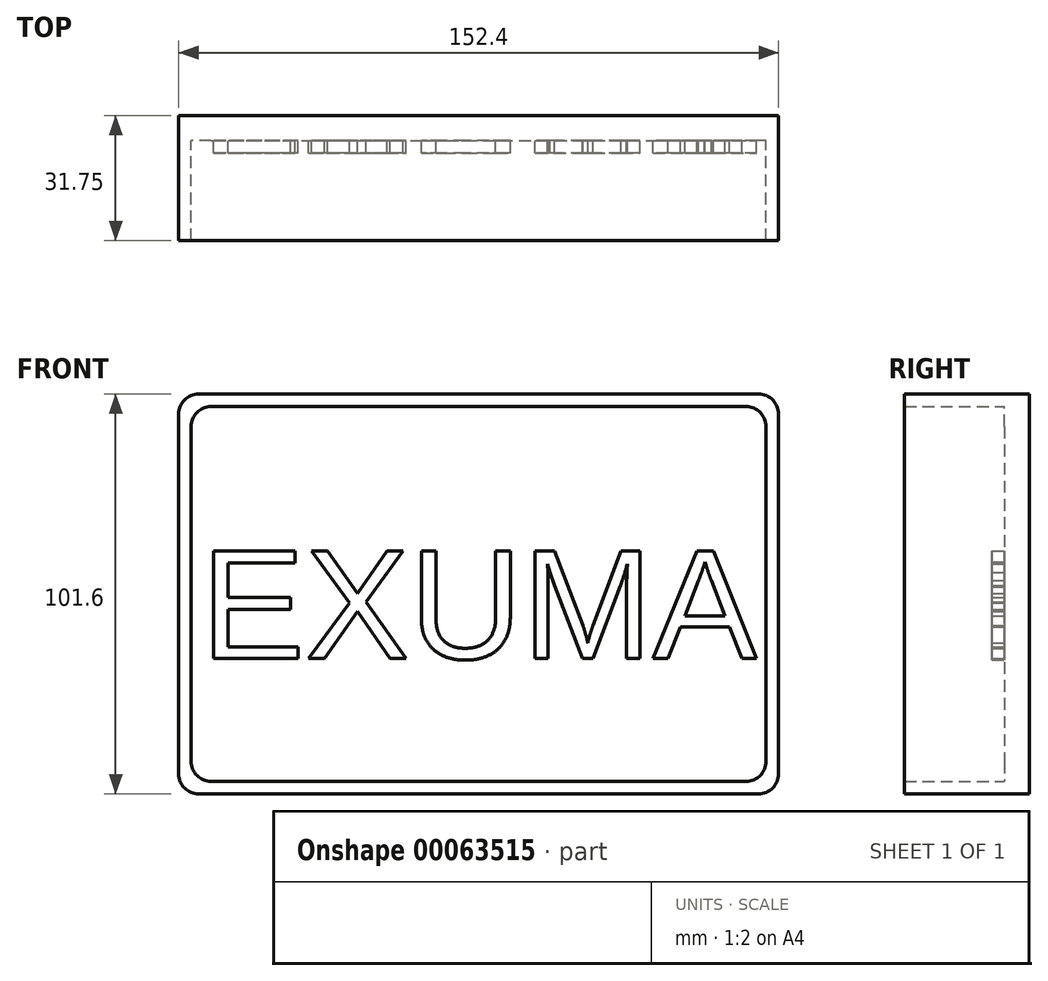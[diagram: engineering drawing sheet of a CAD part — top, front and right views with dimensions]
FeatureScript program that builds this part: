
annotation { "Feature Type Name" : "Feature", "Feature Type Description" : "" }
export const myFeature = defineFeature(function(context is Context, id is Id, definition is map)
    precondition{}
    {
        {
            var Q0;
            Q0=qCreatedBy(makeId("Front.planeOp"),FACE);
            var sketch = newSketch(context, id + "F0", { "sketchPlane" : qUnion([Q0])});
            skLineSegment(sketch, "E0.bottom", {"start": v(-70.07, 52.66) * mm, "end": v(82.33, 52.66) * mm});
            skLineSegment(sketch, "E0.top", {"start": v(-70.07, -48.94) * mm, "end": v(82.33, -48.94) * mm});
            skLineSegment(sketch, "E0.left", {"start": v(-70.07, 52.66) * mm, "end": v(-70.07, -48.94) * mm});
            skLineSegment(sketch, "E0.right", {"start": v(82.33, 52.66) * mm, "end": v(82.33, -48.94) * mm});
            skSolve(sketch);
        }
        {
            var Q0;
            Q0 = qSketchRegion(id + "F0", true);
            extrude(context, id + "F1", {"entities" : qUnion([Q0]), "depth" : 6.35 * mm});
        }
        {
            var Q0;
            Q0=makeQuery(id+"F1.opExtrude","CAP_FACE",FACE,{"disambiguationData":[OSD([sQuery(id+"F0.wireOp",EDGE,"E0.bottom"),sQuery(id+"F0.wireOp",EDGE,"E0.top"),sQuery(id+"F0.wireOp",EDGE,"E0.left"),sQuery(id+"F0.wireOp",EDGE,"E0.right")])],"isStart":false});
            var sketch = newSketch(context, id + "F2", { "sketchPlane" : qUnion([Q0])});
            skLineSegment(sketch, "E1.bottom", {"start": v(-70.07, 52.66) * mm, "end": v(82.33, 52.66) * mm});
            skLineSegment(sketch, "E1.top", {"start": v(-70.07, -48.94) * mm, "end": v(82.33, -48.94) * mm});
            skLineSegment(sketch, "E1.left", {"start": v(-70.07, 52.66) * mm, "end": v(-70.07, -48.94) * mm});
            skLineSegment(sketch, "E1.right", {"start": v(82.33, 52.66) * mm, "end": v(82.33, -48.94) * mm});
            skLineSegment(sketch, "E2.0", {"start": v(-66.9, 49.48) * mm, "end": v(79.16, 49.48) * mm});
            skLineSegment(sketch, "E2.1", {"start": v(-66.9, 49.48) * mm, "end": v(-66.9, -45.77) * mm});
            skLineSegment(sketch, "E2.2", {"start": v(-66.9, -45.77) * mm, "end": v(79.16, -45.77) * mm});
            skLineSegment(sketch, "E2.3", {"start": v(79.16, 49.48) * mm, "end": v(79.16, -45.77) * mm});
            skSolve(sketch);
        }
        {
            var Q0;
            Q0 = qSketchRegion(id + "F2", true);
            extrude(context, id + "F3", {"entities" : qUnion([Q0]), "operationType" : NewBodyOperationType.ADD, "depth" : 25.4 * mm});
        }
        {
            var Q0;
            Q0=makeQuery(id+"F3.boolean.opBoolean","MERGE",EDGE,{"derivedFrom":[makeQuery(id+"F1.opExtrude","SWEPT_EDGE",EDGE,{"disambiguationData":[OSD([sQuery(id+"F0.wireOp",EDGE,"E0.top"),sQuery(id+"F0.wireOp",EDGE,"E0.left")])]}),makeQuery(id+"F3.opExtrude","SWEPT_EDGE",EDGE,{"disambiguationData":[OSD([sQuery(id+"F2.wireOp",EDGE,"E1.top"),sQuery(id+"F2.wireOp",EDGE,"E1.left")])]})]});
            var Q1;
            Q1=makeQuery(id+"F3.opExtrude","SWEPT_EDGE",EDGE,{"disambiguationData":[OSD([sQuery(id+"F2.wireOp",EDGE,"E2.1"),sQuery(id+"F2.wireOp",EDGE,"E2.2")])]});
            var Q2;
            Q2=makeQuery(id+"F3.opExtrude","SWEPT_EDGE",EDGE,{"disambiguationData":[OSD([sQuery(id+"F2.wireOp",EDGE,"E2.0"),sQuery(id+"F2.wireOp",EDGE,"E2.1")])]});
            var Q3;
            Q3=makeQuery(id+"F3.boolean.opBoolean","MERGE",EDGE,{"derivedFrom":[makeQuery(id+"F1.opExtrude","SWEPT_EDGE",EDGE,{"disambiguationData":[OSD([sQuery(id+"F0.wireOp",EDGE,"E0.bottom"),sQuery(id+"F0.wireOp",EDGE,"E0.left")])]}),makeQuery(id+"F3.opExtrude","SWEPT_EDGE",EDGE,{"disambiguationData":[OSD([sQuery(id+"F2.wireOp",EDGE,"E1.bottom"),sQuery(id+"F2.wireOp",EDGE,"E1.left")])]})]});
            var Q4;
            Q4=makeQuery(id+"F3.boolean.opBoolean","MERGE",EDGE,{"derivedFrom":[makeQuery(id+"F1.opExtrude","SWEPT_EDGE",EDGE,{"disambiguationData":[OSD([sQuery(id+"F0.wireOp",EDGE,"E0.top"),sQuery(id+"F0.wireOp",EDGE,"E0.right")])]}),makeQuery(id+"F3.opExtrude","SWEPT_EDGE",EDGE,{"disambiguationData":[OSD([sQuery(id+"F2.wireOp",EDGE,"E1.top"),sQuery(id+"F2.wireOp",EDGE,"E1.right")])]})]});
            var Q5;
            Q5=makeQuery(id+"F3.opExtrude","SWEPT_EDGE",EDGE,{"disambiguationData":[OSD([sQuery(id+"F2.wireOp",EDGE,"E2.2"),sQuery(id+"F2.wireOp",EDGE,"E2.3")])]});
            var Q6;
            Q6=makeQuery(id+"F3.boolean.opBoolean","MERGE",EDGE,{"derivedFrom":[makeQuery(id+"F1.opExtrude","SWEPT_EDGE",EDGE,{"disambiguationData":[OSD([sQuery(id+"F0.wireOp",EDGE,"E0.bottom"),sQuery(id+"F0.wireOp",EDGE,"E0.right")])]}),makeQuery(id+"F3.opExtrude","SWEPT_EDGE",EDGE,{"disambiguationData":[OSD([sQuery(id+"F2.wireOp",EDGE,"E1.bottom"),sQuery(id+"F2.wireOp",EDGE,"E1.right")])]})]});
            var Q7;
            Q7=makeQuery(id+"F3.opExtrude","SWEPT_EDGE",EDGE,{"disambiguationData":[OSD([sQuery(id+"F2.wireOp",EDGE,"E2.0"),sQuery(id+"F2.wireOp",EDGE,"E2.3")])]});
            fillet(context, id + "F4", {"entities" : qUnion([Q0, Q1, Q2, Q3, Q4, Q5, Q6, Q7]), "radius" : 5.08 * mm, "tangentPropagation" : true, "allowEdgeOverflow" : false});
        }
        {
            var Q0;
            Q0=makeQuery(id+"F1.opExtrude","CAP_FACE",FACE,{"disambiguationData":[OSD([sQuery(id+"F0.wireOp",EDGE,"E0.bottom"),sQuery(id+"F0.wireOp",EDGE,"E0.top"),sQuery(id+"F0.wireOp",EDGE,"E0.left"),sQuery(id+"F0.wireOp",EDGE,"E0.right")])],"isStart":false});
            var sketch = newSketch(context, id + "F5", { "sketchPlane" : qUnion([Q0])});
            skText(sketch, "E3", { "text": "EXUMA", "fontName": "Arimo-Regular.ttf"});
            const initialGuessF5  = {"E3": [-0.06448, -0.01456, 1, 0, 0.02861]};
            skSetInitialGuess(sketch, initialGuessF5);
            skSolve(sketch);
        }
        {
            var Q0;
            Q0 = qSketchRegion(id + "F5", true);
            extrude(context, id + "F6", {"entities" : qUnion([Q0]), "operationType" : NewBodyOperationType.ADD, "depth" : 3.17 * mm});
        }
    });
